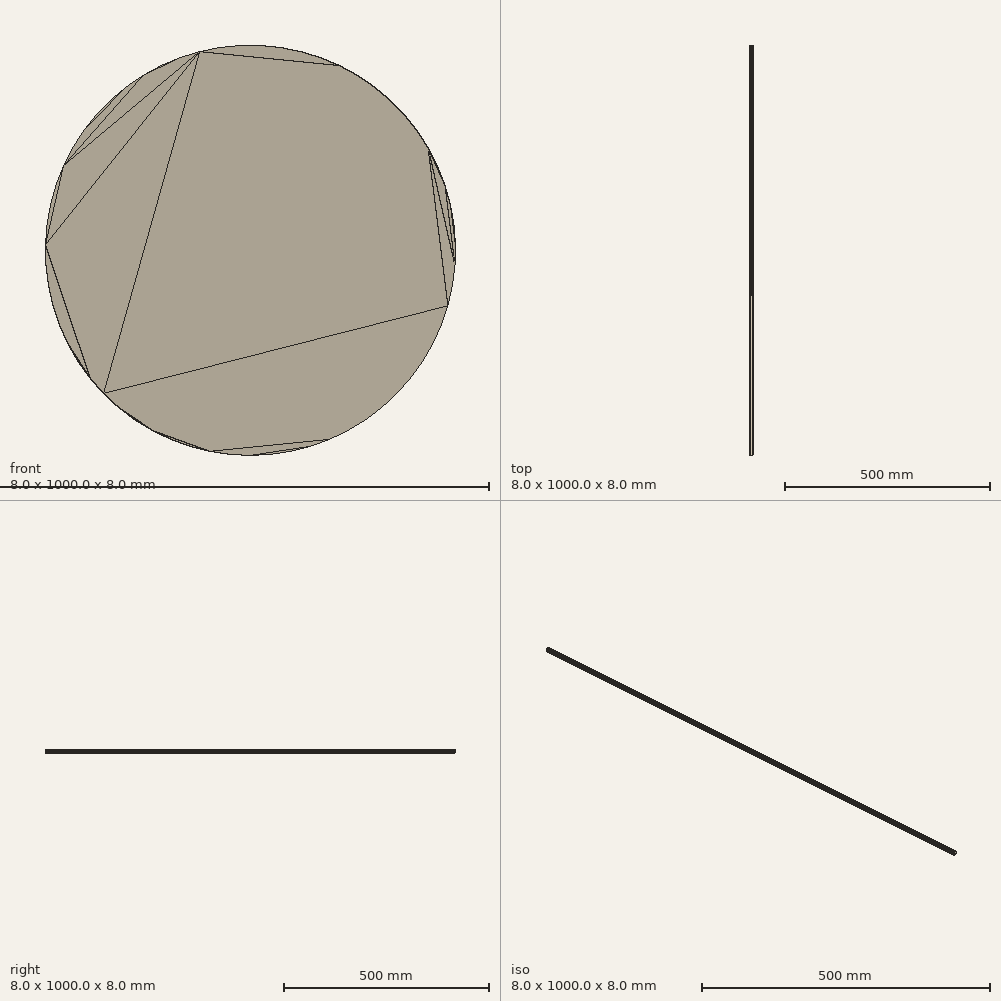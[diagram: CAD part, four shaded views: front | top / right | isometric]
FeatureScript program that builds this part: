
annotation { "Feature Type Name" : "Feature", "Feature Type Description" : "" }
export const myFeature = defineFeature(function(context is Context, id is Id, definition is map)
    precondition{}
    {
        {
            var Q0;
            Q0=qCreatedBy(makeId("Front.planeOp"),FACE);
            var sketch = newSketch(context, id + "F0", { "sketchPlane" : qUnion([Q0])});
            skCircle(sketch, "E0", {"center": v(0, 0) * mm, "radius": 4 * mm});
            skSolve(sketch);
        }
        {
            var Q0;
            Q0 = qSketchRegion(id + "F0", true);
            extrude(context, id + "F1", {"entities" : qUnion([Q0]), "depth" : 1000 * mm});
        }
    });
